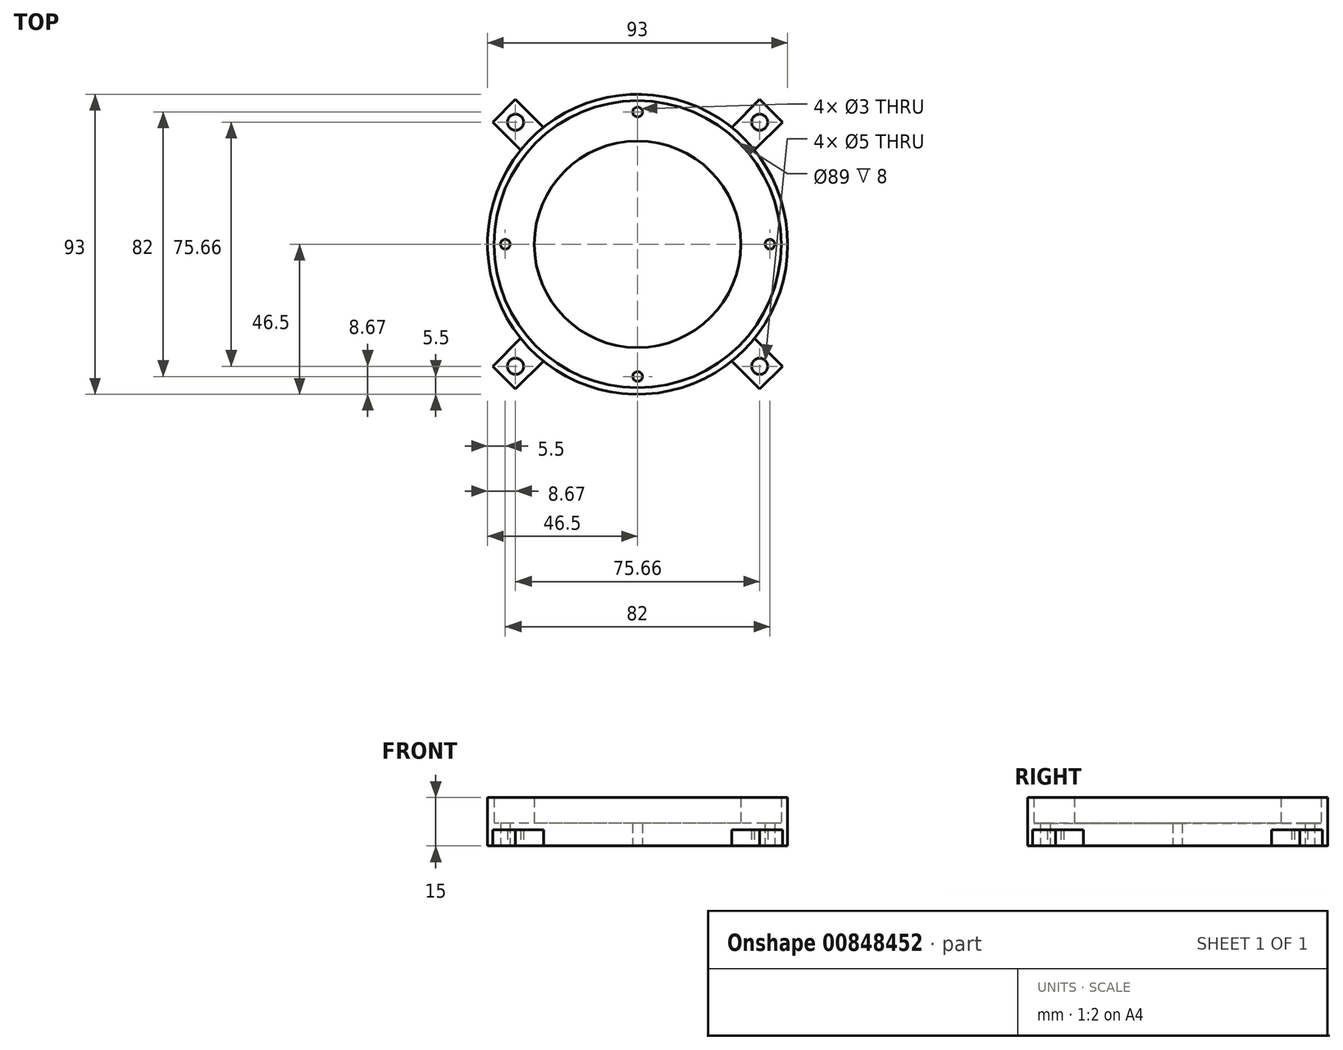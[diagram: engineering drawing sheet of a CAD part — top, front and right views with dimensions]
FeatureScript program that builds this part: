
annotation { "Feature Type Name" : "Feature", "Feature Type Description" : "" }
export const myFeature = defineFeature(function(context is Context, id is Id, definition is map)
    precondition{}
    {
        {
            var Q0;
            Q0=qCreatedBy(makeId("Top.planeOp"),FACE);
            var sketch = newSketch(context, id + "F0", { "sketchPlane" : qUnion([Q0])});
            skCircle(sketch, "E0", {"center": v(0, 0) * mm, "radius": 32.5 * mm, "construction": true});
            skCircle(sketch, "E1", {"center": v(0, 0) * mm, "radius": 44 * mm, "construction": true});
            skCircle(sketch, "E2", {"center": v(0, 41) * mm, "radius": 1.5 * mm});
            skCircle(sketch, "E3", {"center": v(-41, 0) * mm, "radius": 1.5 * mm});
            skCircle(sketch, "E4", {"center": v(0, -41) * mm, "radius": 1.5 * mm});
            skCircle(sketch, "E5", {"center": v(41, 0) * mm, "radius": 1.5 * mm});
            skCircle(sketch, "E6", {"center": v(0, 0) * mm, "radius": 32 * mm});
            skCircle(sketch, "E7", {"center": v(0, 0) * mm, "radius": 44.5 * mm});
            skCircle(sketch, "E8", {"center": v(0, 0) * mm, "radius": 46.5 * mm});
            skLineSegment(sketch, "E9", {"start": v(0, 0) * mm, "end": v(58.53, 58.53) * mm, "construction": true});
            skLineSegment(sketch, "E10", {"start": v(0, 0) * mm, "end": v(-59.63, -59.63) * mm, "construction": true});
            skLineSegment(sketch, "E11", {"start": v(0, 0) * mm, "end": v(-58.64, 58.64) * mm, "construction": true});
            skLineSegment(sketch, "E12", {"start": v(0, 0) * mm, "end": v(61.95, -61.95) * mm, "construction": true});
            skCircle(sketch, "E13", {"center": v(-37.83, -37.83) * mm, "radius": 2.5 * mm});
            skCircle(sketch, "E14", {"center": v(-37.83, 37.83) * mm, "radius": 2.5 * mm});
            skCircle(sketch, "E15", {"center": v(37.83, 37.83) * mm, "radius": 2.5 * mm});
            skCircle(sketch, "E16", {"center": v(37.83, -37.83) * mm, "radius": 2.5 * mm});
            skLineSegment(sketch, "E17", {"start": v(-29.15, 36.23) * mm, "end": v(-37.83, 44.9) * mm});
            skLineSegment(sketch, "E18", {"start": v(-37.83, 44.9) * mm, "end": v(-44.9, 37.83) * mm});
            skLineSegment(sketch, "E19", {"start": v(-44.9, 37.83) * mm, "end": v(-36.23, 29.15) * mm});
            skLineSegment(sketch, "E20", {"start": v(36.23, 29.15) * mm, "end": v(44.9, 37.83) * mm});
            skLineSegment(sketch, "E21", {"start": v(44.9, 37.83) * mm, "end": v(37.83, 44.9) * mm});
            skLineSegment(sketch, "E22", {"start": v(37.83, 44.9) * mm, "end": v(29.15, 36.23) * mm});
            skLineSegment(sketch, "E23", {"start": v(29.15, -36.23) * mm, "end": v(37.83, -44.9) * mm});
            skLineSegment(sketch, "E24", {"start": v(37.83, -44.9) * mm, "end": v(44.9, -37.83) * mm});
            skLineSegment(sketch, "E25", {"start": v(44.9, -37.83) * mm, "end": v(36.23, -29.15) * mm});
            skLineSegment(sketch, "E26", {"start": v(-29.15, -36.23) * mm, "end": v(-37.83, -44.9) * mm});
            skLineSegment(sketch, "E27", {"start": v(-37.83, -44.9) * mm, "end": v(-44.9, -37.83) * mm});
            skLineSegment(sketch, "E28", {"start": v(-44.9, -37.83) * mm, "end": v(-36.23, -29.15) * mm});
            skSolve(sketch);
        }
        {
            var Q0;
            Q0=makeQuery(id+"F0.imprint","IMPRINT",FACE,{"disambiguationData":[TD([[makeQuery(id+"F0.imprint","IMPRINT",EDGE,{"derivedFrom":sQuery(id+"F0.wireOp",EDGE,"E2")}),-1.0]])]});
            extrude(context, id + "F1", {"entities" : qUnion([Q0]), "depth" : 7 * mm, "offsetDistance" : 25 * mm});
        }
        {
            var Q0;
            Q0=makeQuery(id+"F0.imprint","IMPRINT",FACE,{"disambiguationData":[TD([[makeQuery(id+"F0.imprint","IMPRINT",EDGE,{"derivedFrom":sQuery(id+"F0.wireOp",EDGE,"E6")}),1.0]])]});
            var Q1;
            Q1=makeQuery(id+"F0.imprint","IMPRINT",FACE,{"disambiguationData":[TD([[makeQuery(id+"F0.imprint","IMPRINT",EDGE,{"derivedFrom":sQuery(id+"F0.wireOp",EDGE,"E7")}),-1.0]])]});
            extrude(context, id + "F2", {"entities" : qUnion([Q0, Q1]), "operationType" : NewBodyOperationType.ADD, "depth" : 15 * mm, "offsetDistance" : 25 * mm});
        }
        {
            var Q0;
            Q0=makeQuery(id+"F0.imprint","IMPRINT",FACE,{"disambiguationData":[TD([[makeQuery(id+"F0.imprint","IMPRINT",EDGE,{"derivedFrom":sQuery(id+"F0.wireOp",EDGE,"E13")}),-1.0]])]});
            var Q1;
            Q1=makeQuery(id+"F0.imprint","IMPRINT",FACE,{"disambiguationData":[TD([[makeQuery(id+"F0.imprint","IMPRINT",EDGE,{"derivedFrom":sQuery(id+"F0.wireOp",EDGE,"E14")}),-1.0]])]});
            var Q2;
            Q2=makeQuery(id+"F0.imprint","IMPRINT",FACE,{"disambiguationData":[TD([[makeQuery(id+"F0.imprint","IMPRINT",EDGE,{"derivedFrom":sQuery(id+"F0.wireOp",EDGE,"E15")}),-1.0]])]});
            var Q3;
            Q3=makeQuery(id+"F0.imprint","IMPRINT",FACE,{"disambiguationData":[TD([[makeQuery(id+"F0.imprint","IMPRINT",EDGE,{"derivedFrom":sQuery(id+"F0.wireOp",EDGE,"E16")}),-1.0]])]});
            extrude(context, id + "F3", {"entities" : qUnion([Q0, Q1, Q2, Q3]), "operationType" : NewBodyOperationType.ADD, "depth" : 5 * mm, "offsetDistance" : 25 * mm});
        }
    });
